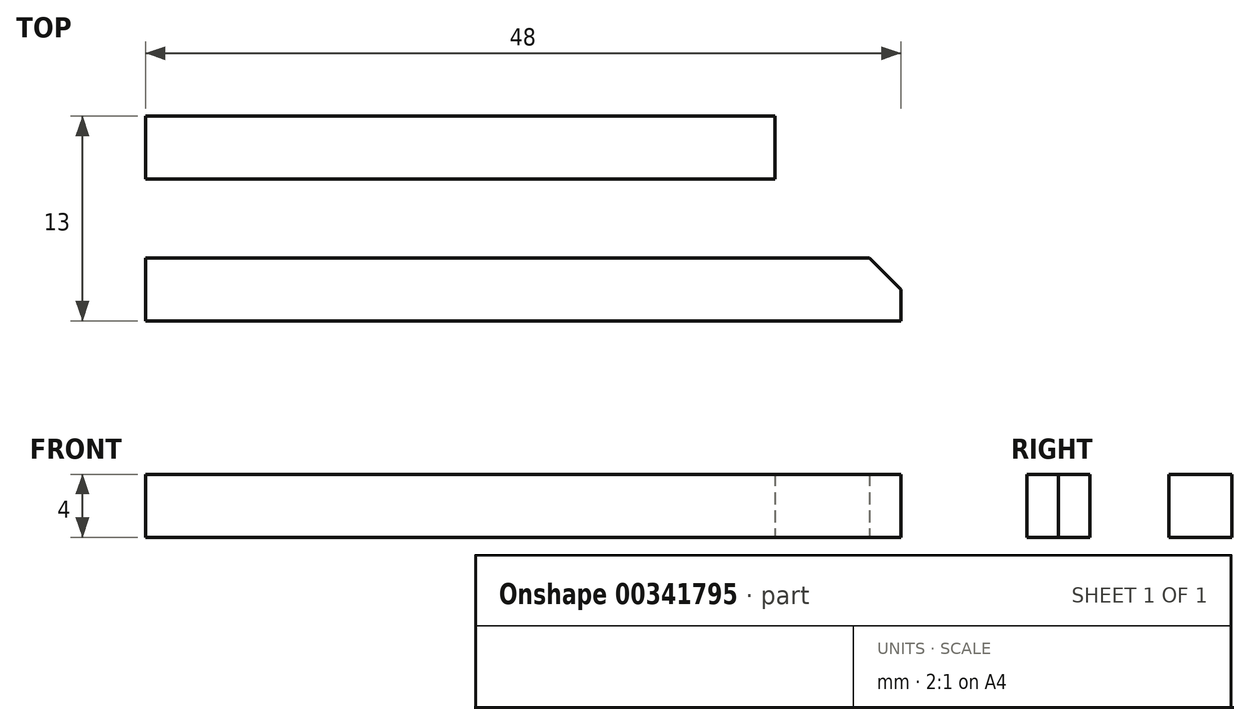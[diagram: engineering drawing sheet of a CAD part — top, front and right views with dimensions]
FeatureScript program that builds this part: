
annotation { "Feature Type Name" : "Feature", "Feature Type Description" : "" }
export const myFeature = defineFeature(function(context is Context, id is Id, definition is map)
    precondition{}
    {
        {
            var Q0;
            Q0=qCreatedBy(makeId("Top.planeOp"),FACE);
            var sketch = newSketch(context, id + "F0", { "sketchPlane" : qUnion([Q0])});
            skLineSegment(sketch, "E0.bottom", {"start": v(-23, 2.38) * mm, "end": v(17, 2.38) * mm});
            skLineSegment(sketch, "E0.top", {"start": v(-23, 6.38) * mm, "end": v(17, 6.38) * mm});
            skLineSegment(sketch, "E0.left", {"start": v(-23, 2.38) * mm, "end": v(-23, 6.38) * mm});
            skLineSegment(sketch, "E0.right", {"start": v(17, 2.38) * mm, "end": v(17, 6.38) * mm});
            skLineSegment(sketch, "E1.bottom", {"start": v(-23, 2.38) * mm, "end": v(-19, 2.38) * mm});
            skLineSegment(sketch, "E1.top", {"start": v(-23, -2.62) * mm, "end": v(-19, -2.62) * mm});
            skLineSegment(sketch, "E1.left", {"start": v(-23, 2.38) * mm, "end": v(-23, -2.62) * mm});
            skLineSegment(sketch, "E1.right", {"start": v(-19, 2.38) * mm, "end": v(-19, -2.62) * mm});
            skLineSegment(sketch, "E2.bottom", {"start": v(-23, -2.62) * mm, "end": v(25, -2.62) * mm});
            skLineSegment(sketch, "E2.top", {"start": v(-23, -6.62) * mm, "end": v(25, -6.62) * mm});
            skLineSegment(sketch, "E2.left", {"start": v(-23, -2.62) * mm, "end": v(-23, -6.62) * mm});
            skLineSegment(sketch, "E2.right", {"start": v(25, -2.62) * mm, "end": v(25, -6.62) * mm});
            skLineSegment(sketch, "E3.bottom", {"start": v(25, -2.62) * mm, "end": v(21, -2.62) * mm});
            skLineSegment(sketch, "E3.top", {"start": v(25, 3.35) * mm, "end": v(21, 3.35) * mm});
            skLineSegment(sketch, "E3.left", {"start": v(25, -2.62) * mm, "end": v(25, 3.35) * mm});
            skLineSegment(sketch, "E3.right", {"start": v(21, -2.62) * mm, "end": v(21, 3.35) * mm});
            skSolve(sketch);
        }
        {
            var Q0;
            Q0=makeQuery(id+"F0.imprint","IMPRINT",FACE,{"disambiguationData":[TD([[makeQuery(id+"F0.imprint","IMPRINT",EDGE,{"derivedFrom":sQuery(id+"F0.wireOp",EDGE,"E1.bottom")}),-1.0]])]});
            var Q1;
            Q1=makeQuery(id+"F0.imprint","IMPRINT",FACE,{"disambiguationData":[TD([[makeQuery(id+"F0.imprint","IMPRINT",EDGE,{"derivedFrom":sQuery(id+"F0.wireOp",EDGE,"E2.top")}),1.0]])]});
            var Q2;
            Q2=makeQuery(id+"F0.imprint","IMPRINT",FACE,{"disambiguationData":[TD([[makeQuery(id+"F0.imprint","IMPRINT",EDGE,{"derivedFrom":sQuery(id+"F0.wireOp",EDGE,"E0.bottom")}),1.0]])]});
            var Q3;
            Q3=makeQuery(id+"F0.imprint","IMPRINT",FACE,{"disambiguationData":[TD([[makeQuery(id+"F0.imprint","IMPRINT",EDGE,{"derivedFrom":sQuery(id+"F0.wireOp",EDGE,"E3.bottom")}),-1.0]])]});
            extrude(context, id + "F1", {"entities" : qUnion([Q0, Q1, Q2, Q3]), "depth" : 4 * mm});
        }
        {
            var Q0;
            Q0=makeQuery(id+"F1.opExtrude","SWEPT_EDGE",EDGE,{"disambiguationData":[OSD([sQuery(id+"F0.wireOp",EDGE,"E3.top"),sQuery(id+"F0.wireOp",EDGE,"E3.right")])]});
            var Q1;
            Q1=makeQuery(id+"F1.opExtrude","SWEPT_EDGE",EDGE,{"disambiguationData":[OSD([sQuery(id+"F0.wireOp",EDGE,"E3.top"),sQuery(id+"F0.wireOp",EDGE,"E3.left")])]});
            chamfer(context, id + "F2", {"entities" : qUnion([Q0, Q1]), "width" : 2 * mm, "tangentPropagation" : true});
        }
    });
